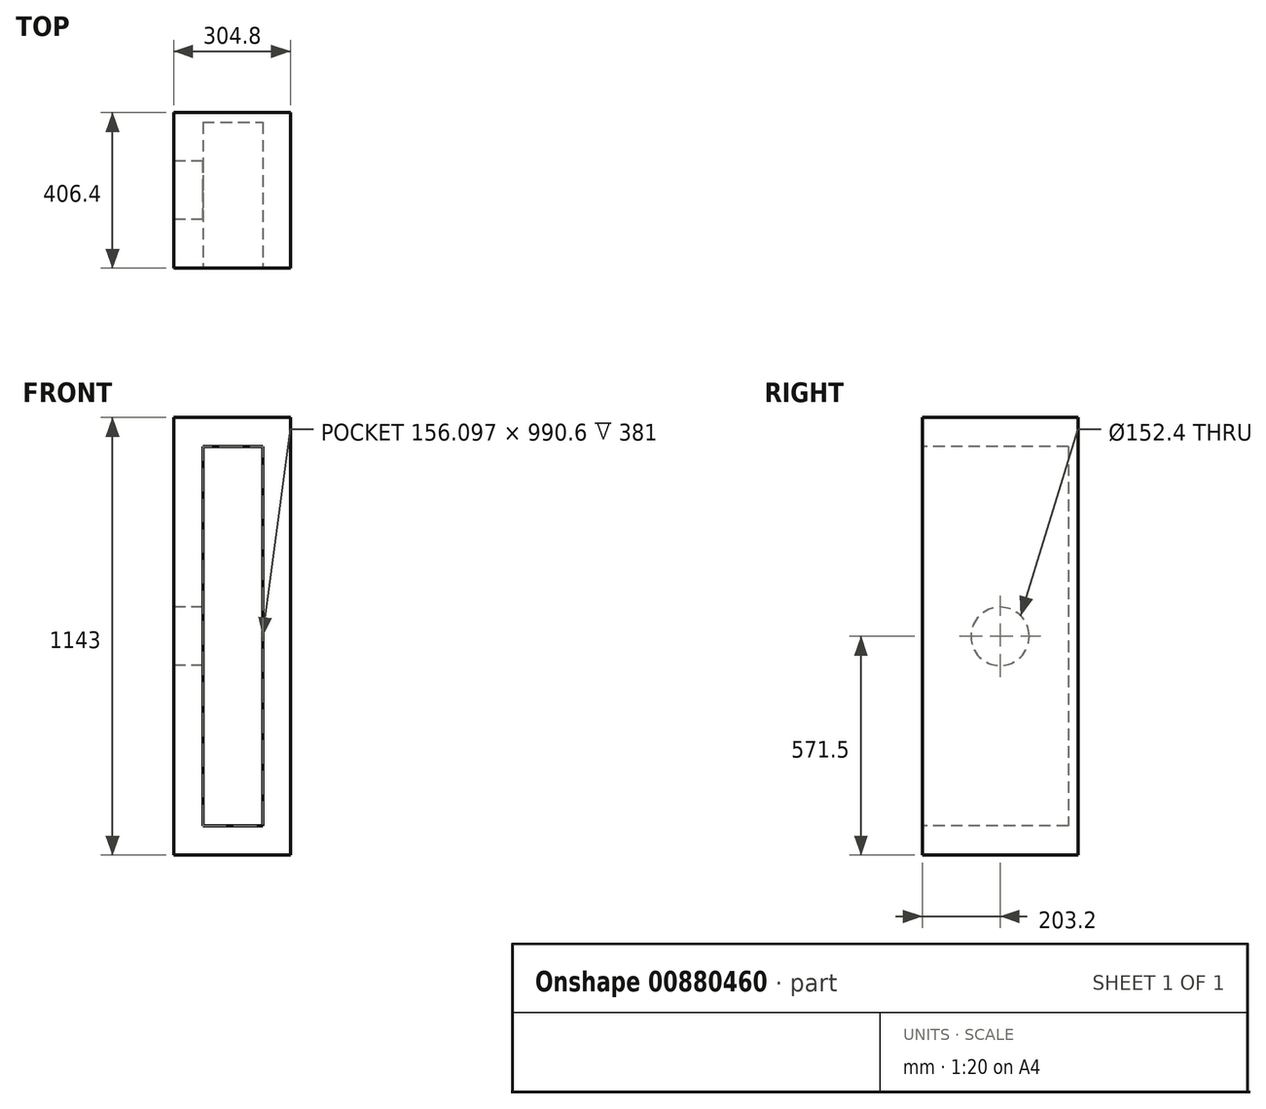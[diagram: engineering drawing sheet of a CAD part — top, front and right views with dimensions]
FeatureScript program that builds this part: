
annotation { "Feature Type Name" : "Feature", "Feature Type Description" : "" }
export const myFeature = defineFeature(function(context is Context, id is Id, definition is map)
    precondition{}
    {
        {
            var Q0;
            Q0=qCreatedBy(makeId("Front.planeOp"),FACE);
            var sketch = newSketch(context, id + "F0", { "sketchPlane" : qUnion([Q0])});
            skLineSegment(sketch, "E0.bottom", {"start": v(152.4, -571.5) * mm, "end": v(-152.4, -571.5) * mm});
            skLineSegment(sketch, "E0.top", {"start": v(152.4, 571.5) * mm, "end": v(-152.4, 571.5) * mm});
            skLineSegment(sketch, "E0.left", {"start": v(152.4, -571.5) * mm, "end": v(152.4, 571.5) * mm});
            skLineSegment(sketch, "E0.right", {"start": v(-152.4, -571.5) * mm, "end": v(-152.4, 571.5) * mm});
            skPoint(sketch, "E0.middle", {"position": v(0, 0) * mm});
            skSolve(sketch);
        }
        {
            var Q0;
            Q0 = qSketchRegion(id + "F0", true);
            extrude(context, id + "F1", {"entities" : qUnion([Q0]), "depth" : 406.4 * mm, "offsetDistance" : 25.4 * mm});
        }
        {
            var Q0;
            Q0=makeQuery(id+"F1.opExtrude","CAP_FACE",FACE,{"disambiguationData":[OSD([sQuery(id+"F0.wireOp",EDGE,"E0.bottom"),sQuery(id+"F0.wireOp",EDGE,"E0.top"),sQuery(id+"F0.wireOp",EDGE,"E0.left"),sQuery(id+"F0.wireOp",EDGE,"E0.right")])],"isStart":false});
            var sketch = newSketch(context, id + "F2", { "sketchPlane" : qUnion([Q0])});
            skLineSegment(sketch, "E1", {"start": v(-152.4, 571.5) * mm, "end": v(-76.2, 571.5) * mm, "construction": true});
            skLineSegment(sketch, "E2", {"start": v(-152.4, 571.5) * mm, "end": v(-152.4, 495.3) * mm, "construction": true});
            skLineSegment(sketch, "E3.bottom", {"start": v(-76.2, 495.3) * mm, "end": v(79.9, 495.3) * mm});
            skLineSegment(sketch, "E3.top", {"start": v(-76.2, -495.3) * mm, "end": v(79.9, -495.3) * mm});
            skLineSegment(sketch, "E3.left", {"start": v(-76.2, 495.3) * mm, "end": v(-76.2, -495.3) * mm});
            skLineSegment(sketch, "E3.right", {"start": v(79.9, 495.3) * mm, "end": v(79.9, -495.3) * mm});
            skSolve(sketch);
        }
        {
            var Q0;
            Q0 = qSketchRegion(id + "F2", true);
            extrude(context, id + "F3", {"entities" : qUnion([Q0]), "operationType" : NewBodyOperationType.REMOVE, "oppositeDirection" : true, "depth" : 381 * mm, "offsetDistance" : 25.4 * mm});
        }
        {
            var Q0;
            Q0=makeQuery(id+"F1.opExtrude","SWEPT_FACE",FACE,{"disambiguationData":[OSD([sQuery(id+"F0.wireOp",EDGE,"E0.right")])]});
            var sketch = newSketch(context, id + "F4", { "sketchPlane" : qUnion([Q0])});
            skCircle(sketch, "E4", {"center": v(203.2, 0) * mm, "radius": 76.2 * mm});
            skPoint(sketch, "E4.centerSnap0", {"position": v(203.2, 571.5) * mm});
            skSolve(sketch);
        }
        {
            var Q0;
            Q0 = qSketchRegion(id + "F4", true);
            extrude(context, id + "F5", {"entities" : qUnion([Q0]), "operationType" : NewBodyOperationType.REMOVE, "oppositeDirection" : true, "depth" : 76.2 * mm, "offsetDistance" : 25.4 * mm});
        }
    });
